# Revit family: 1RLV-CX_Straight_DN15_RFA
name_source: partatom
category: Pipe Accessories
units: mm (PartAtom-declared; Revit-internal decimal feet)

## family parameters
Always vertical = Yes
Cut with Voids When Loaded = No
OmniClass Number = 23.65.55.14.17
OmniClass Title = Adjusting/Controlling Valves for Liquid Services
Part Type = Valve - Breaks Into
Round Connector Dimension = Use Diameter
Shared = No
Work Plane-Based = No

## types (1)
- RLV-CX_Straight_DN15_003L0274
    CenSd_S11_6 = 13.1 mm
    CenSd_S22_6 = 15 mm  [stored 0.0492126 ft]
    D = 15 mm  [stored 0.0492126 ft]
    D1 = 0 mm  [stored 0 ft]
    D2 = 19 mm  [stored 0.062336 ft]
    D4 = 21 mm  [stored 0.0688976 ft]
    D5 = 21 mm  [stored 0.0688976 ft]
    D6 = 26.5 mm  [stored 0.0869423 ft]
    Description = Lockshield Valve
    H2 = 20 mm  [stored 0.0656168 ft]
    HT = 38.2 mm  [stored 0.125328 ft]
    IfcExportAs = IfcValveType
    IfcExportType = RLV-CX
    Kvs = 2.5 m³/h
    L2 = 20.5 mm  [stored 0.0672572 ft]
    L3 = 5 mm  [stored 0.0164042 ft]
    L4 = 3.53 mm
    L5 = 13.84 mm  [stored 0.0454068 ft]
    LL = 32 mm  [stored 0.104987 ft]
    LL1 = 28.1 mm  [stored 0.0921916 ft]
    LL2 = 60.1 mm  [stored 0.197178 ft]
    LOD 200 = No
    LOD 350 = Yes
    Manufacturer = Danfoss
    Max Medium Temperature = 120 ˚C
    Max Operating Pressure = 10 bar
    Model = 003L0274
    Model Type = RLV-CX_Straight_DN15
    R2 = 12.17 mm  [stored 0.0399278 ft]
    RB = 15 mm  [stored 0.0492126 ft]
    RD2 = 9.5 mm  [stored 0.031168 ft]
    RD5 = 10.5 mm  [stored 0.0344488 ft]
    RV1 = 10.47 mm  [stored 0.0343504 ft]
    R_thread1 = 15 mm  [stored 0.0492126 ft]
    S11 = 15.13 mm  [stored 0.0496391 ft]
    S22 = 17.32 mm
    T2 = 5.7 mm  [stored 0.0187008 ft]
    URL = https://store.danfoss.com
    Valve Body Material = Danfoss Brass (Chrome plated)
    W2D = 10 mm  [stored 0.0328084 ft]
    Weight = 0.25 kg
    X = 11.5 mm  [stored 0.0377297 ft]
    X1 = 10.67 mm
    X1__ve = -10.67 mm
    X2 = 39.2 mm
    X5 = -10.5 mm  [stored -0.0344488 ft]

note: [stored X ft] marks values corroborated as IEEE doubles in the binary element streams (Revit-internal decimal feet)

## geometry (parser evidence)
native form markers: Sweep x4
no freeform markers — native parametric forms only
